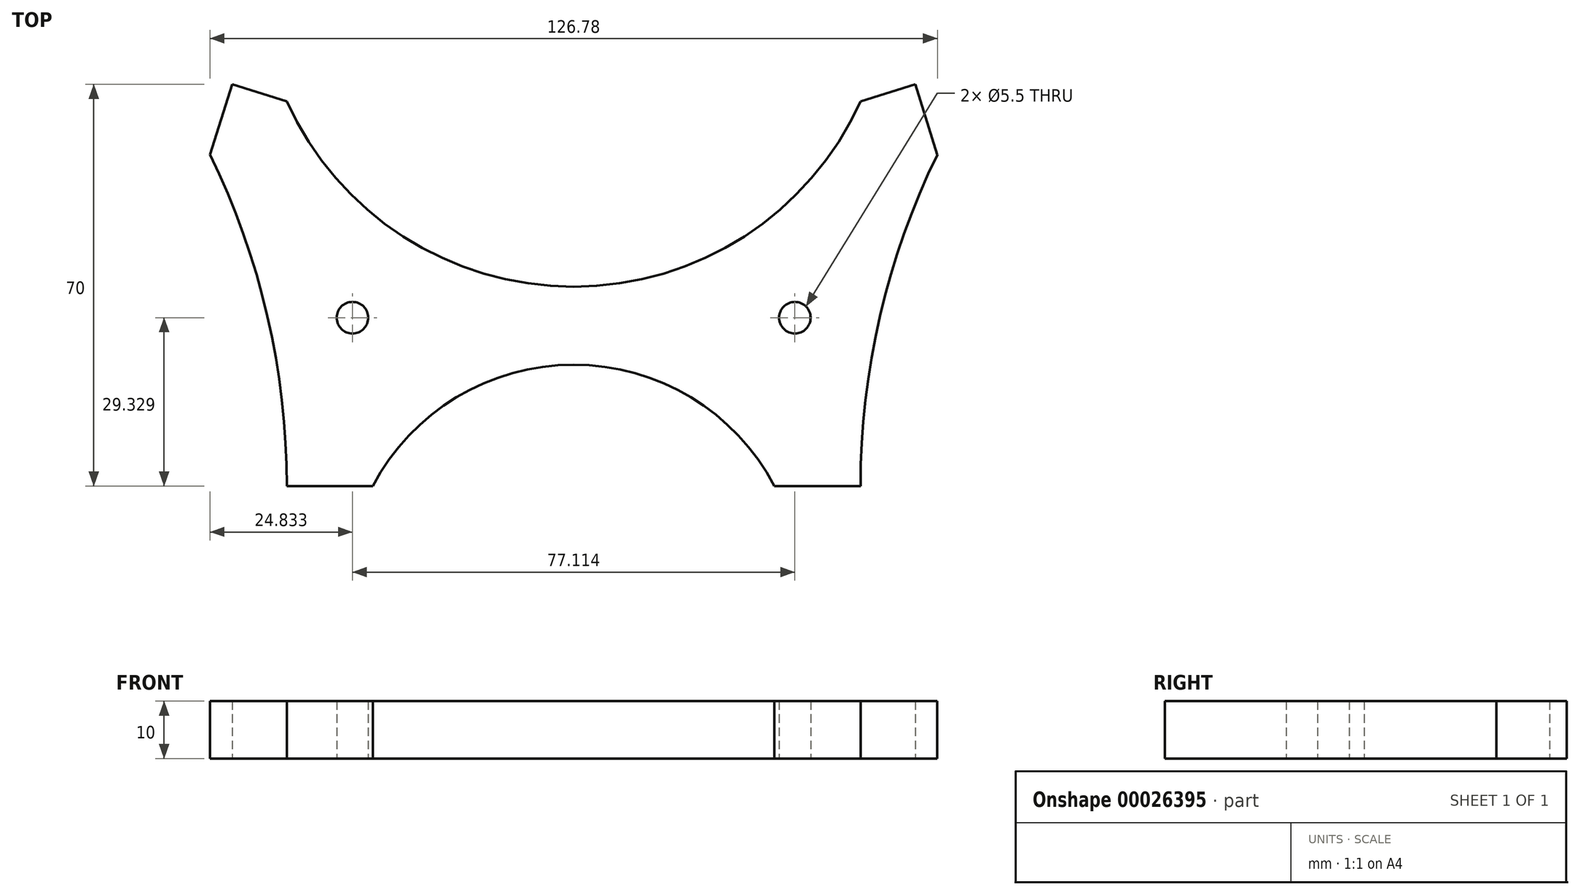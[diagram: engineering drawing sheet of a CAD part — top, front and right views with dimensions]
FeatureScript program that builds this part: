
annotation { "Feature Type Name" : "Feature", "Feature Type Description" : "" }
export const myFeature = defineFeature(function(context is Context, id is Id, definition is map)
    precondition{}
    {
        {
            var Q0;
            Q0=qCreatedBy(makeId("Top.planeOp"),FACE);
            var sketch = newSketch(context, id + "F0", { "sketchPlane" : qUnion([Q0])});
            skLineSegment(sketch, "E0", {"start": v(70, 22) * mm, "end": v(0, 0) * mm, "construction": true});
            skLineSegment(sketch, "E1", {"start": v(59.54, 18.71) * mm, "end": v(50, 15.71) * mm});
            skArc(sketch, "E2", {"start": v(0, -16.56) * mm, "mid": v(29.76, -7.79) * mm, "end": v(50, 15.71) * mm});
            skLineSegment(sketch, "E3", {"start": v(59.54, 18.71) * mm, "end": v(63.39, 6.46) * mm});
            skLineSegment(sketch, "E4", {"start": v(35, -51.29) * mm, "end": v(50, -51.29) * mm});
            skArc(sketch, "E5", {"start": v(35, -51.29) * mm, "mid": v(20.44, -35.85) * mm, "end": v(0, -30.16) * mm});
            skArc(sketch, "E6", {"start": v(63.39, 6.46) * mm, "mid": v(53.4, -21.65) * mm, "end": v(50, -51.29) * mm});
            skCircle(sketch, "E7", {"center": v(38.56, -21.96) * mm, "radius": 2.75 * mm});
            skArc(sketch, "E8.MirrorCS", {"start": v(0, -16.56) * mm, "mid": v(-29.76, -7.79) * mm, "end": v(-50, 15.71) * mm});
            skLineSegment(sketch, "E9.MirrorCS", {"start": v(-59.54, 18.71) * mm, "end": v(-50, 15.71) * mm});
            skLineSegment(sketch, "E10.MirrorCS", {"start": v(-59.54, 18.71) * mm, "end": v(-63.39, 6.46) * mm});
            skArc(sketch, "E11.MirrorCS", {"start": v(-63.39, 6.46) * mm, "mid": v(-53.4, -21.65) * mm, "end": v(-50, -51.29) * mm});
            skLineSegment(sketch, "E12.MirrorCS", {"start": v(-35, -51.29) * mm, "end": v(-50, -51.29) * mm});
            skArc(sketch, "E13.MirrorCS", {"start": v(-35, -51.29) * mm, "mid": v(-20.44, -35.85) * mm, "end": v(0, -30.16) * mm});
            skCircle(sketch, "E14.MirrorC", {"center": v(-38.56, -21.96) * mm, "radius": 2.75 * mm});
            skSolve(sketch);
        }
        {
            var Q0;
            Q0=makeQuery(id+"F0.imprint","IMPRINT",FACE,{"disambiguationData":[TD([[makeQuery(id+"F0.imprint","IMPRINT",EDGE,{"derivedFrom":sQuery(id+"F0.wireOp",EDGE,"E1")}),1.0]])]});
            extrude(context, id + "F1", {"entities" : qUnion([Q0]), "depth" : 10 * mm});
        }
    });
